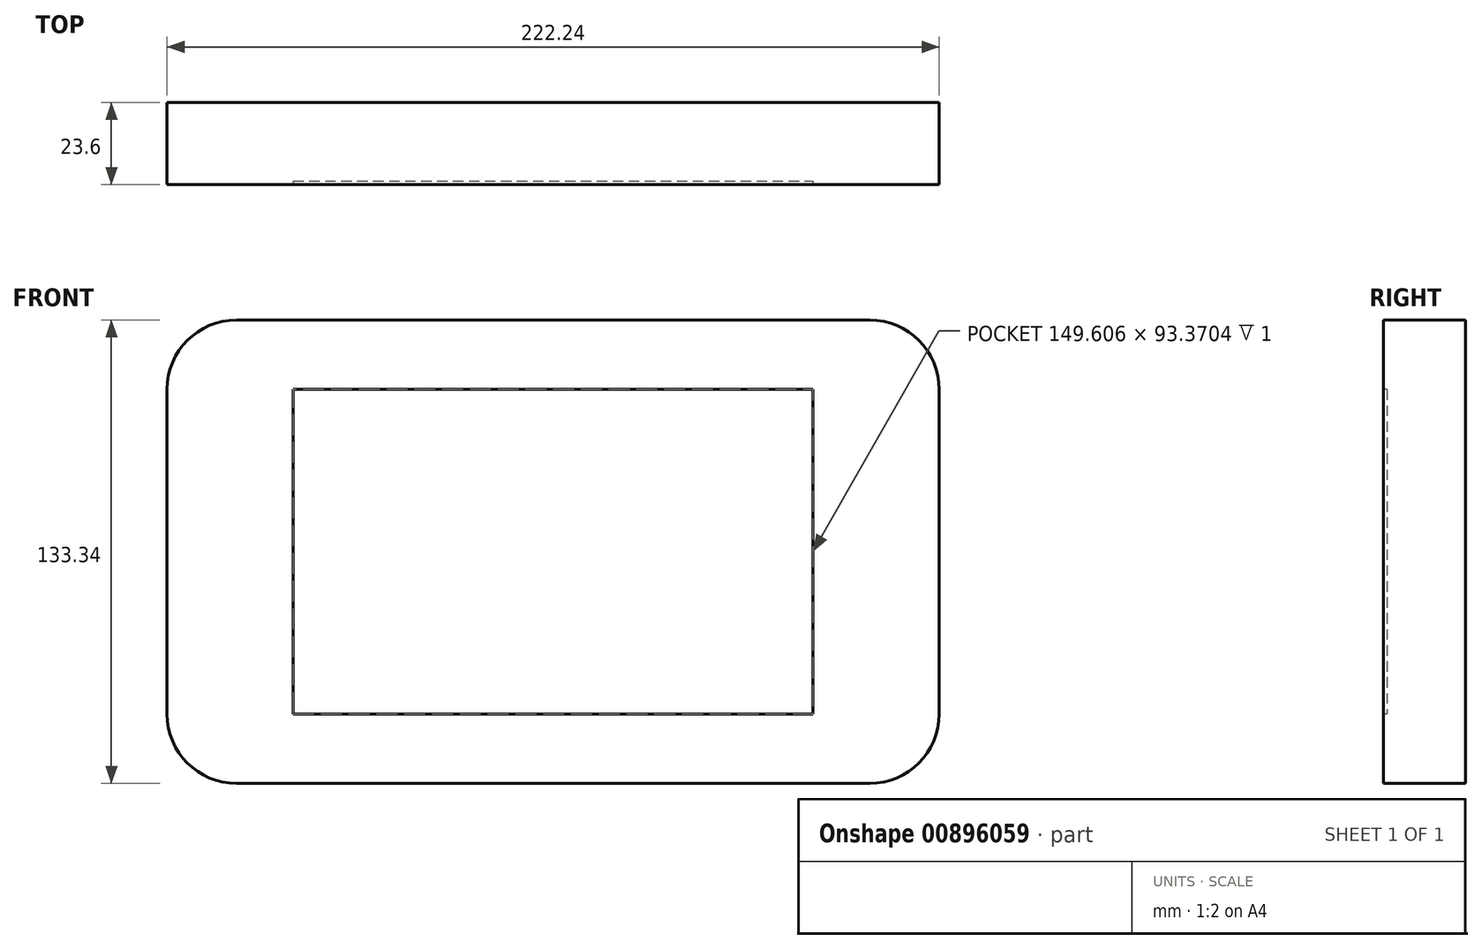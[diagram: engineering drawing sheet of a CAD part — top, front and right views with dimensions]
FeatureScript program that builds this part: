
annotation { "Feature Type Name" : "Feature", "Feature Type Description" : "" }
export const myFeature = defineFeature(function(context is Context, id is Id, definition is map)
    precondition{}
    {
        {
            var Q0;
            Q0=qCreatedBy(makeId("Front.planeOp"),FACE);
            var sketch = newSketch(context, id + "F0", { "sketchPlane" : qUnion([Q0])});
            skLineSegment(sketch, "E0", {"start": v(-91.12, 66.67) * mm, "end": v(91.12, 66.67) * mm});
            skArc(sketch, "E1", {"start": v(91.12, 66.68) * mm, "mid": v(105.27, 60.82) * mm, "end": v(111.12, 46.68) * mm});
            skLineSegment(sketch, "E2", {"start": v(111.13, 46.68) * mm, "end": v(111.13, -46.68) * mm});
            skArc(sketch, "E3", {"start": v(111.13, -46.68) * mm, "mid": v(105.27, -60.82) * mm, "end": v(91.12, -66.68) * mm});
            skLineSegment(sketch, "E4", {"start": v(91.12, -66.67) * mm, "end": v(-91.12, -66.67) * mm});
            skArc(sketch, "E5", {"start": v(-91.13, 66.68) * mm, "mid": v(-105.27, 60.82) * mm, "end": v(-111.13, 46.68) * mm});
            skArc(sketch, "E6", {"start": v(-91.12, -66.68) * mm, "mid": v(-105.27, -60.82) * mm, "end": v(-111.12, -46.68) * mm});
            skLineSegment(sketch, "E7", {"start": v(-111.12, 46.68) * mm, "end": v(-111.12, -46.68) * mm});
            skLineSegment(sketch, "E8", {"start": v(-91.13, 46.68) * mm, "end": v(91.13, -46.68) * mm, "construction": true});
            skLineSegment(sketch, "E9", {"start": v(0, 66.67) * mm, "end": v(0, -66.67) * mm, "construction": true});
            skLineSegment(sketch, "E10", {"start": v(111.13, 0) * mm, "end": v(-111.12, 0) * mm, "construction": true});
            skLineSegment(sketch, "E11", {"start": v(-91.13, 46.68) * mm, "end": v(-91.13, 66.67) * mm, "construction": true});
            skLineSegment(sketch, "E12", {"start": v(-111.12, 46.68) * mm, "end": v(-91.12, 46.68) * mm, "construction": true});
            skLineSegment(sketch, "E13", {"start": v(91.13, 46.68) * mm, "end": v(91.13, 66.68) * mm, "construction": true});
            skLineSegment(sketch, "E14", {"start": v(91.12, 46.68) * mm, "end": v(111.12, 46.68) * mm, "construction": true});
            skLineSegment(sketch, "E15", {"start": v(91.12, -66.68) * mm, "end": v(91.12, -46.68) * mm, "construction": true});
            skLineSegment(sketch, "E16", {"start": v(111.12, -46.68) * mm, "end": v(91.12, -46.68) * mm, "construction": true});
            skLineSegment(sketch, "E17", {"start": v(-91.12, -66.68) * mm, "end": v(-91.12, -46.68) * mm, "construction": true});
            skLineSegment(sketch, "E18", {"start": v(-111.12, -46.68) * mm, "end": v(-91.12, -46.68) * mm, "construction": true});
            skSolve(sketch);
        }
        {
            var Q0;
            Q0 = qSketchRegion(id + "F0", true);
            extrude(context, id + "F1", {"entities" : qUnion([Q0]), "depth" : 23.6 * mm, "offsetDistance" : 25 * mm});
        }
        {
            var Q0;
            Q0=makeQuery(id+"F1.opExtrude","CAP_FACE",FACE,{"disambiguationData":[OSD([sQuery(id+"F0.wireOp",EDGE,"E0"),sQuery(id+"F0.wireOp",EDGE,"E1"),sQuery(id+"F0.wireOp",EDGE,"E2"),sQuery(id+"F0.wireOp",EDGE,"E3"),sQuery(id+"F0.wireOp",EDGE,"E4"),sQuery(id+"F0.wireOp",EDGE,"E5"),sQuery(id+"F0.wireOp",EDGE,"E6"),sQuery(id+"F0.wireOp",EDGE,"E7")])],"isStart":false});
            var sketch = newSketch(context, id + "F2", { "sketchPlane" : qUnion([Q0])});
            skLineSegment(sketch, "E19.bottom", {"start": v(-74.8, 46.69) * mm, "end": v(74.8, 46.69) * mm});
            skLineSegment(sketch, "E19.top", {"start": v(-74.8, -46.69) * mm, "end": v(74.8, -46.69) * mm});
            skLineSegment(sketch, "E19.left", {"start": v(-74.8, 46.69) * mm, "end": v(-74.8, -46.69) * mm});
            skLineSegment(sketch, "E19.right", {"start": v(74.8, 46.69) * mm, "end": v(74.8, -46.69) * mm});
            skLineSegment(sketch, "E20", {"start": v(-74.8, 46.69) * mm, "end": v(74.8, -46.69) * mm, "construction": true});
            skSolve(sketch);
        }
        {
            var Q0;
            Q0 = qSketchRegion(id + "F2", true);
            extrude(context, id + "F3", {"entities" : qUnion([Q0]), "operationType" : NewBodyOperationType.REMOVE, "oppositeDirection" : true, "depth" : 1 * mm, "offsetDistance" : 25 * mm});
        }
    });
